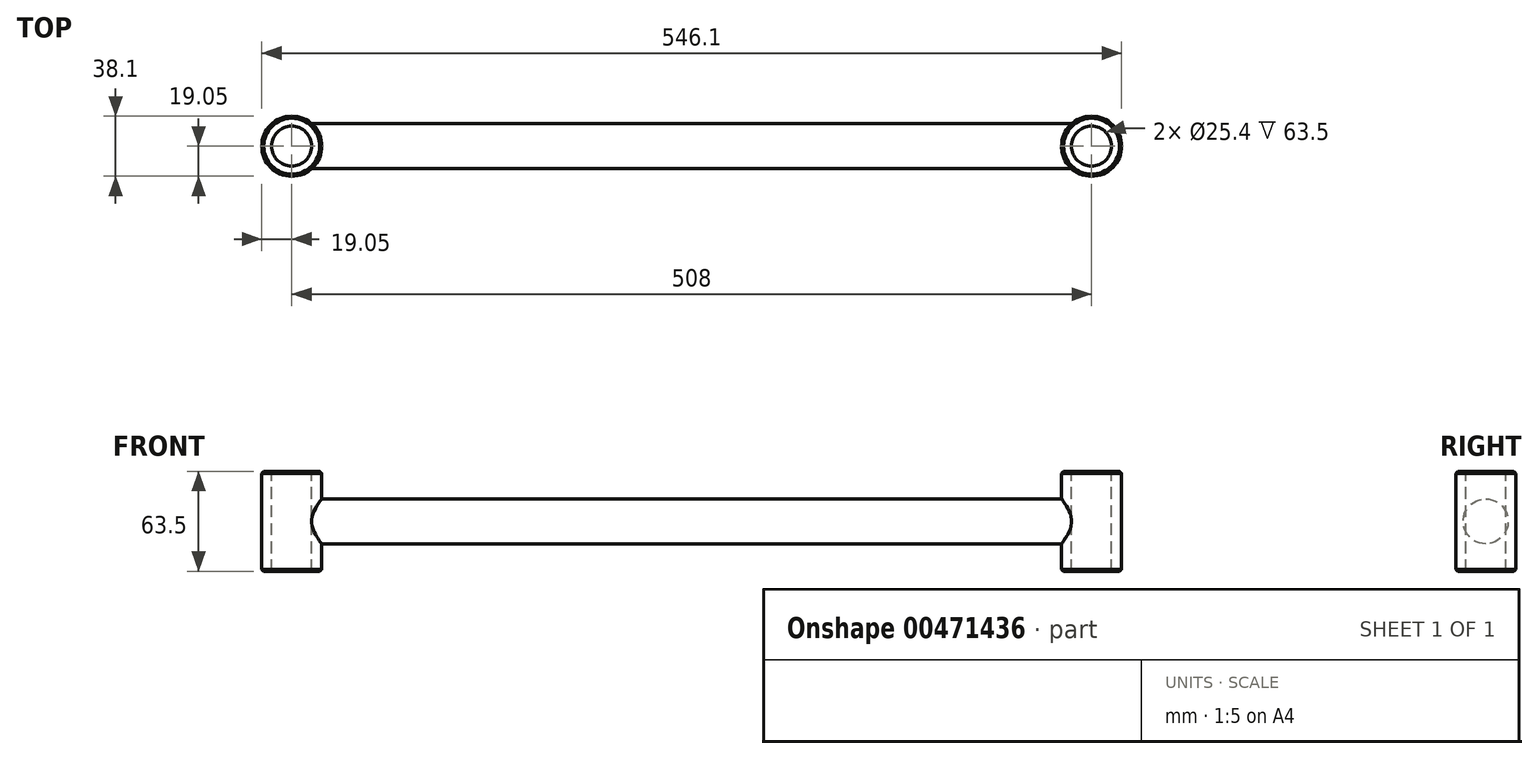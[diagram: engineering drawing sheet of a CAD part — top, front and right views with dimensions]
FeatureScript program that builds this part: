
annotation { "Feature Type Name" : "Feature", "Feature Type Description" : "" }
export const myFeature = defineFeature(function(context is Context, id is Id, definition is map)
    precondition{}
    {
        {
            var Q0;
            Q0=qCreatedBy(makeId("Top.planeOp"),FACE);
            var sketch = newSketch(context, id + "F0", { "sketchPlane" : qUnion([Q0])});
            skCircle(sketch, "E0", {"center": v(0, 0) * mm, "radius": 19.05 * mm});
            skCircle(sketch, "E1", {"center": v(508, 0) * mm, "radius": 19.05 * mm});
            skSolve(sketch);
        }
        {
            var Q0;
            Q0=makeQuery(id+"F0.imprint","IMPRINT",FACE,{"disambiguationData":[TD([[makeQuery(id+"F0.imprint","IMPRINT",EDGE,{"derivedFrom":sQuery(id+"F0.wireOp",EDGE,"E0")}),1.0]])]});
            var Q1;
            Q1=makeQuery(id+"F0.imprint","IMPRINT",FACE,{"disambiguationData":[TD([[makeQuery(id+"F0.imprint","IMPRINT",EDGE,{"derivedFrom":sQuery(id+"F0.wireOp",EDGE,"E1")}),1.0]])]});
            extrude(context, id + "F1", {"entities" : qUnion([Q0, Q1]), "depth" : 63.5 * mm});
        }
        {
            var Q0;
            Q0=qCreatedBy(makeId("Front.planeOp"),FACE);
            var sketch = newSketch(context, id + "F2", { "sketchPlane" : qUnion([Q0])});
            skLineSegment(sketch, "E2", {"start": v(0, 31.75) * mm, "end": v(508, 31.75) * mm});
            skSolve(sketch);
        }
        {
            var Q0;
            Q0=qCreatedBy(makeId("Right.planeOp"),FACE);
            var sketch = newSketch(context, id + "F3", { "sketchPlane" : qUnion([Q0])});
            skCircle(sketch, "E3", {"center": v(0, 31.75) * mm, "radius": 14.29 * mm});
            skSolve(sketch);
        }
        {
            var Q0;
            Q0=makeQuery(id+"F3.imprint","IMPRINT",FACE,{"disambiguationData":[TD([[makeQuery(id+"F3.imprint","IMPRINT",EDGE,{"derivedFrom":sQuery(id+"F3.wireOp",EDGE,"E3")}),1.0]])]});
            var Q1;
            Q1=sQuery(id+"F2.wireOp",EDGE,"E2");
            sweep(context, id + "F4", {"operationType" : NewBodyOperationType.ADD, "profiles" : qUnion([Q0]), "path" : qUnion([Q1])});
        }
        {
            var Q0;
            Q0=makeQuery(id+"F1.opExtrude","CAP_FACE",FACE,{"disambiguationData":[OSD([sQuery(id+"F0.wireOp",EDGE,"E0")])],"isStart":false});
            var sketch = newSketch(context, id + "F5", { "sketchPlane" : qUnion([Q0])});
            skCircle(sketch, "E4", {"center": v(0, 0) * mm, "radius": 12.7 * mm});
            skCircle(sketch, "E5", {"center": v(508, 0) * mm, "radius": 12.7 * mm});
            skSolve(sketch);
        }
        {
            var Q0;
            Q0 = qSketchRegion(id + "F5", true);
            extrude(context, id + "F6", {"entities" : qUnion([Q0]), "operationType" : NewBodyOperationType.REMOVE, "oppositeDirection" : true, "depth" : 63.5 * mm});
        }
        {
            var Q0;
            Q0=makeQuery(id+"F1.opExtrude","CAP_EDGE",EDGE,{"disambiguationData":[OSD([sQuery(id+"F0.wireOp",EDGE,"E0")])],"isStart":false});
            var Q1;
            Q1=makeQuery(id+"F6.boolean.opBoolean","COPY",EDGE,{"derivedFrom":makeQuery(id+"F6.opExtrude","CAP_EDGE",EDGE,{"disambiguationData":[OSD([sQuery(id+"F5.wireOp",EDGE,"E4")])],"isStart":true})});
            var Q2;
            Q2=makeQuery(id+"F1.opExtrude","CAP_EDGE",EDGE,{"disambiguationData":[OSD([sQuery(id+"F0.wireOp",EDGE,"E0")])],"isStart":true});
            var Q3;
            Q3=makeQuery(id+"F6.boolean.opBoolean","COPY",EDGE,{"derivedFrom":makeQuery(id+"F6.opExtrude","CAP_EDGE",EDGE,{"disambiguationData":[OSD([sQuery(id+"F5.wireOp",EDGE,"E4")])],"isStart":false})});
            var Q4;
            Q4=makeQuery(id+"F1.opExtrude","CAP_EDGE",EDGE,{"disambiguationData":[OSD([sQuery(id+"F0.wireOp",EDGE,"E1")])],"isStart":true});
            var Q5;
            Q5=makeQuery(id+"F6.boolean.opBoolean","COPY",EDGE,{"derivedFrom":makeQuery(id+"F6.opExtrude","CAP_EDGE",EDGE,{"disambiguationData":[OSD([sQuery(id+"F5.wireOp",EDGE,"E5")])],"isStart":false})});
            var Q6;
            Q6=makeQuery(id+"F6.boolean.opBoolean","COPY",EDGE,{"derivedFrom":makeQuery(id+"F6.opExtrude","CAP_EDGE",EDGE,{"disambiguationData":[OSD([sQuery(id+"F5.wireOp",EDGE,"E5")])],"isStart":true})});
            var Q7;
            Q7=makeQuery(id+"F1.opExtrude","CAP_EDGE",EDGE,{"disambiguationData":[OSD([sQuery(id+"F0.wireOp",EDGE,"E1")])],"isStart":false});
            chamfer(context, id + "F7", {"entities" : qUnion([Q0, Q1, Q2, Q3, Q4, Q5, Q6, Q7]), "width" : 1.27 * mm, "tangentPropagation" : true});
        }
    });
